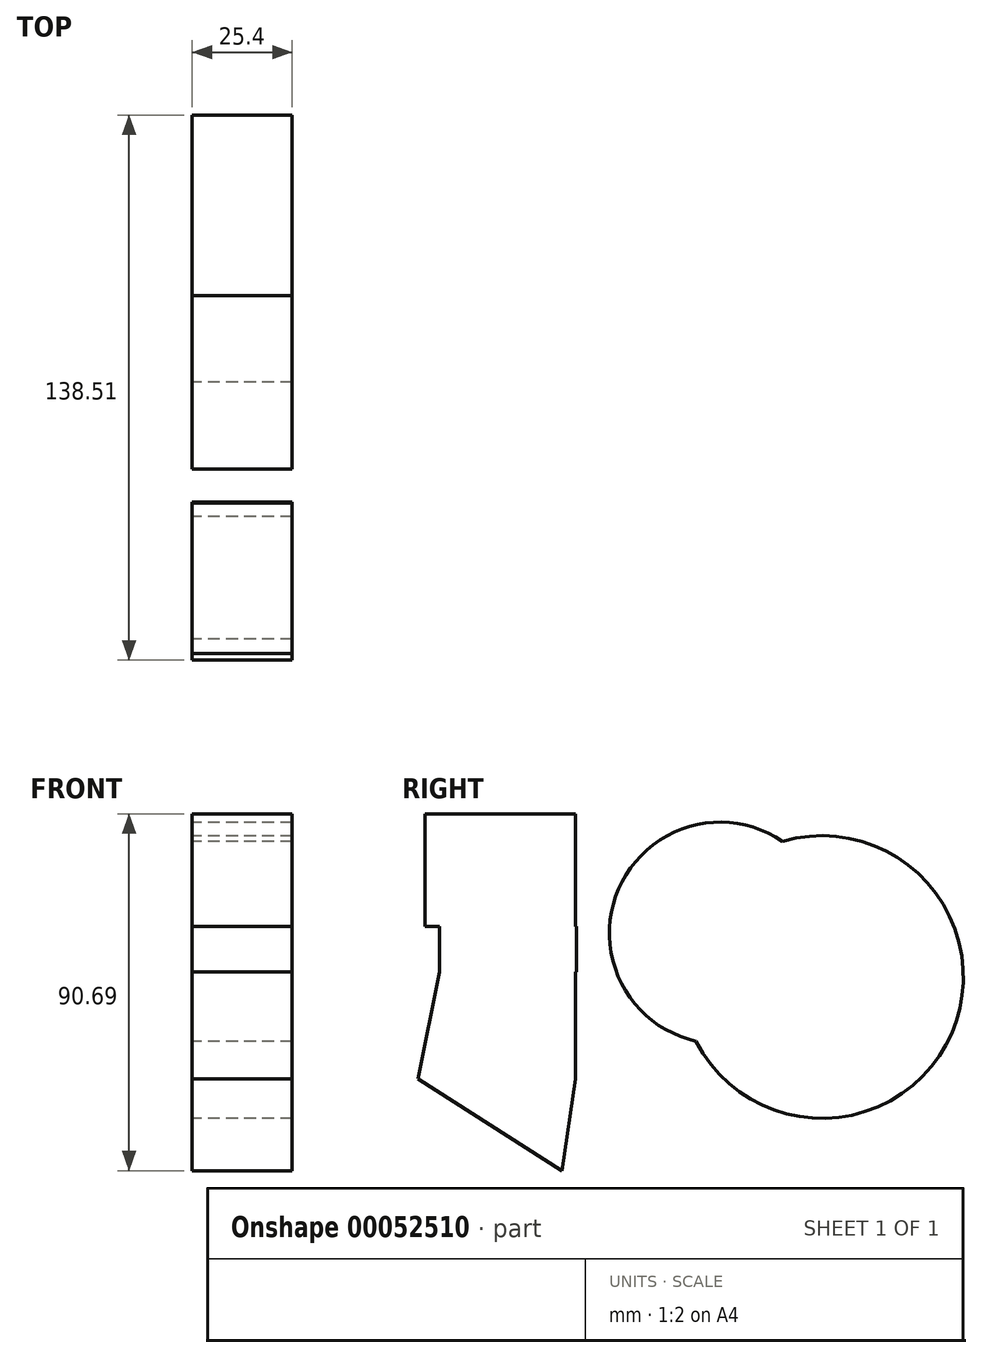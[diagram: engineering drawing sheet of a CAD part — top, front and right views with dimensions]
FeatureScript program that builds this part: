
annotation { "Feature Type Name" : "Feature", "Feature Type Description" : "" }
export const myFeature = defineFeature(function(context is Context, id is Id, definition is map)
    precondition{}
    {
        {
            var Q0;
            Q0=qCreatedBy(makeId("Right.planeOp"),FACE);
            var sketch = newSketch(context, id + "F0", { "sketchPlane" : qUnion([Q0])});
            skLineSegment(sketch, "E0", {"start": v(-56.65, 0) * mm, "end": v(-19.88, 0) * mm});
            skLineSegment(sketch, "E1", {"start": v(-19.88, 22.74) * mm, "end": v(-19.88, -16.03) * mm});
            skLineSegment(sketch, "E2", {"start": v(-19.88, -16.03) * mm, "end": v(-59.87, -16.03) * mm});
            skLineSegment(sketch, "E3", {"start": v(-59.87, -16.03) * mm, "end": v(-56.65, 0) * mm});
            skLineSegment(sketch, "E4", {"start": v(-54.43, 11.07) * mm, "end": v(-56.65, 0) * mm});
            skLineSegment(sketch, "E5", {"start": v(-56.65, 0) * mm, "end": v(-59.87, -16.03) * mm});
            skLineSegment(sketch, "E6.bottom", {"start": v(-58.14, 51.31) * mm, "end": v(-19.88, 51.31) * mm});
            skLineSegment(sketch, "E6.top", {"start": v(-58.14, 22.74) * mm, "end": v(-19.88, 22.74) * mm});
            skLineSegment(sketch, "E6.left", {"start": v(-58.14, 51.31) * mm, "end": v(-58.14, 22.74) * mm});
            skLineSegment(sketch, "E6.right", {"start": v(-19.88, 51.31) * mm, "end": v(-19.88, 22.74) * mm});
            skLineSegment(sketch, "E7.bottom", {"start": v(-19.63, 22.74) * mm, "end": v(-54.43, 22.74) * mm});
            skLineSegment(sketch, "E7.top", {"start": v(-19.63, 11.07) * mm, "end": v(-54.43, 11.07) * mm});
            skLineSegment(sketch, "E7.left", {"start": v(-19.63, 22.74) * mm, "end": v(-19.63, 11.07) * mm});
            skLineSegment(sketch, "E7.right", {"start": v(-54.43, 22.74) * mm, "end": v(-54.43, 11.07) * mm});
            skCircle(sketch, "E8", {"center": v(16.9, 21) * mm, "radius": 28.16 * mm});
            skCircle(sketch, "E9", {"center": v(42.74, 9.81) * mm, "radius": 35.9 * mm});
            skLineSegment(sketch, "E10", {"start": v(-59.87, -16.03) * mm, "end": v(-23.36, -39.38) * mm});
            skLineSegment(sketch, "E11", {"start": v(-23.36, -39.38) * mm, "end": v(-19.88, -16.03) * mm});
            skSolve(sketch);
        }
        {
            var Q0;
            {var subQ5=sQuery(id+"F0.wireOp",EDGE,"E7.left");Q0=makeQuery(id+"F0.imprint","IMPRINT",FACE,{"disambiguationData":[TD([[makeQuery(id+"F0.imprint","IMPRINT",EDGE,{"derivedFrom":subQ5}),-1.0]])]});}
            var Q1;
            Q1=makeQuery(id+"F0.imprint","IMPRINT",FACE,{"disambiguationData":[TD([[makeQuery(id+"F0.imprint","IMPRINT",EDGE,{"derivedFrom":sQuery(id+"F0.wireOp",EDGE,"E2")}),1.0]])]});
            var Q2;
            Q2=makeQuery(id+"F0.imprint","IMPRINT",FACE,{"disambiguationData":[TD([[makeQuery(id+"F0.imprint","IMPRINT",EDGE,{"derivedFrom":sQuery(id+"F0.wireOp",EDGE,"E6.bottom")}),-1.0]])]});
            var Q3;
            {var subQ0=sQuery(id+"F0.wireOp",EDGE,"E9");var subQ1=sQuery(id+"F0.wireOp",EDGE,"E8");var subQ2=makeQuery(id+"F0.imprint","INTERSECT",VERTEX,{"disambiguationData":[OD(0.0)],"derivedFrom":[subQ1,subQ0]});Q3=makeQuery(id+"F0.imprint","IMPRINT",FACE,{"disambiguationData":[TD([[makeQuery(id+"F0.imprint","IMPRINT",EDGE,{"disambiguationData":[TD([[subQ2,1.0]])],"derivedFrom":subQ1}),1.0]])]});}
            var Q4;
            {var subQ0=sQuery(id+"F0.wireOp",EDGE,"E9");var subQ1=sQuery(id+"F0.wireOp",EDGE,"E8");var subQ2=makeQuery(id+"F0.imprint","INTERSECT",VERTEX,{"disambiguationData":[OD(0.0)],"derivedFrom":[subQ1,subQ0]});Q4=makeQuery(id+"F0.imprint","IMPRINT",FACE,{"disambiguationData":[TD([[makeQuery(id+"F0.imprint","IMPRINT",EDGE,{"disambiguationData":[TD([[subQ2,-1.0]])],"derivedFrom":subQ1}),-1.0]])]});}
            var Q5;
            {var subQ0=sQuery(id+"F0.wireOp",EDGE,"E0");Q5=makeQuery(id+"F0.imprint","IMPRINT",FACE,{"disambiguationData":[TD([[makeQuery(id+"F0.imprint","IMPRINT",EDGE,{"derivedFrom":subQ0}),1.0]])]});}
            var Q6;
            {var subQ0=sQuery(id+"F0.wireOp",EDGE,"E0");Q6=makeQuery(id+"F0.imprint","IMPRINT",FACE,{"disambiguationData":[TD([[makeQuery(id+"F0.imprint","IMPRINT",EDGE,{"derivedFrom":subQ0}),-1.0]])]});}
            var Q7;
            {var subQ0=sQuery(id+"F0.wireOp",EDGE,"E9");var subQ1=sQuery(id+"F0.wireOp",EDGE,"E8");var subQ2=makeQuery(id+"F0.imprint","INTERSECT",VERTEX,{"disambiguationData":[OD(0.0)],"derivedFrom":[subQ1,subQ0]});Q7=makeQuery(id+"F0.imprint","IMPRINT",FACE,{"disambiguationData":[TD([[makeQuery(id+"F0.imprint","IMPRINT",EDGE,{"disambiguationData":[TD([[subQ2,-1.0]])],"derivedFrom":subQ1}),1.0]])]});}
            var Q8;
            {var subQ5=sQuery(id+"F0.wireOp",EDGE,"E7.right");Q8=makeQuery(id+"F0.imprint","IMPRINT",FACE,{"disambiguationData":[TD([[makeQuery(id+"F0.imprint","IMPRINT",EDGE,{"derivedFrom":subQ5}),1.0]])]});}
            extrude(context, id + "F1", {"entities" : qUnion([Q0, Q1, Q2, Q3, Q4, Q5, Q6, Q7, Q8]), "depth" : 25.4 * mm});
        }
    });
